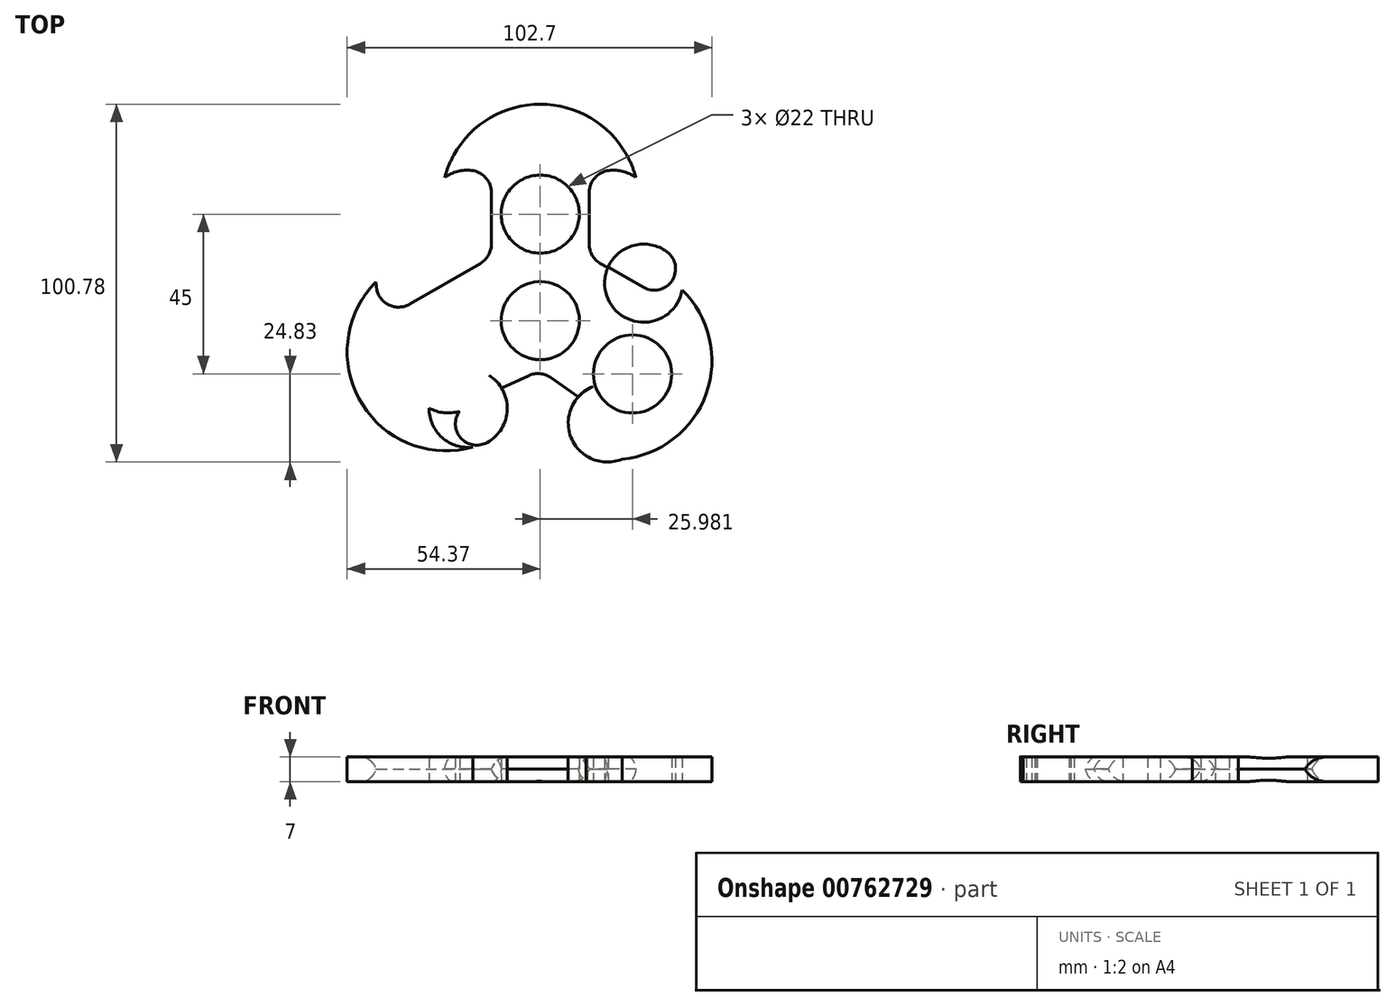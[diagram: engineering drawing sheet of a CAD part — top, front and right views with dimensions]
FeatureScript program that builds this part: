
annotation { "Feature Type Name" : "Feature", "Feature Type Description" : "" }
export const myFeature = defineFeature(function(context is Context, id is Id, definition is map)
    precondition{}
    {
        {
            var Q0;
            Q0=qCreatedBy(makeId("Top.planeOp"),FACE);
            var sketch = newSketch(context, id + "F0", { "sketchPlane" : qUnion([Q0])});
            skCircle(sketch, "E0", {"center": v(0, 0) * mm, "radius": 11 * mm});
            skCircle(sketch, "E1", {"center": v(0, 30) * mm, "radius": 11 * mm});
            skLineSegment(sketch, "E2", {"start": v(0, 30) * mm, "end": v(0, 0) * mm, "construction": true});
            skLineSegment(sketch, "E3", {"start": v(0, 0) * mm, "end": v(25.98, -15) * mm, "construction": true});
            skLineSegment(sketch, "E4", {"start": v(0, 0) * mm, "end": v(-25.98, -15) * mm, "construction": true});
            skCircle(sketch, "E5", {"center": v(-25.98, -15) * mm, "radius": 11 * mm});
            skCircle(sketch, "E6", {"center": v(25.98, -15) * mm, "radius": 11 * mm});
            skLineSegment(sketch, "E7", {"start": v(-36.93, 4.84) * mm, "end": v(-17, 16.35) * mm});
            skLineSegment(sketch, "E8", {"start": v(-20.4, -23.6) * mm, "end": v(-3.15, -15.68) * mm});
            skLineSegment(sketch, "E9", {"start": v(2.83, -16.23) * mm, "end": v(19.2, -27.83) * mm});
            skLineSegment(sketch, "E10", {"start": v(29.1, 9.37) * mm, "end": v(17, 16.35) * mm});
            skLineSegment(sketch, "E11", {"start": v(-14, 36.1) * mm, "end": v(-14, 21.55) * mm});
            skLineSegment(sketch, "E12", {"start": v(14, 36.1) * mm, "end": v(14, 21.55) * mm});
            skPoint(sketch, "E13.visualSharp", {"position": v(-14, 18.08) * mm});
            skArc(sketch, "E13.filletArc", {"start": v(-17, 16.35) * mm, "mid": v(-14.8, 18.55) * mm, "end": v(-14, 21.55) * mm});
            skPoint(sketch, "E14.visualSharp", {"position": v(14, 18.08) * mm});
            skArc(sketch, "E14.filletArc", {"start": v(14, 21.55) * mm, "mid": v(14.8, 18.55) * mm, "end": v(17, 16.35) * mm});
            skPoint(sketch, "E15.visualSharp", {"position": v(0, -14.23) * mm});
            skArc(sketch, "E15.filletArc", {"start": v(2.83, -16.23) * mm, "mid": v(-0.09, -15.15) * mm, "end": v(-3.15, -15.68) * mm});
            skArc(sketch, "E16", {"start": v(-46, 11.15) * mm, "mid": v(-50.64, -22.7) * mm, "end": v(-19, -35.61) * mm});
            skArc(sketch, "E17", {"start": v(12.95, -38.1) * mm, "mid": v(44.6, -25.2) * mm, "end": v(39.95, 8.66) * mm});
            skArc(sketch, "E18", {"start": v(27, 40) * mm, "mid": v(0, 60.95) * mm, "end": v(-27, 40) * mm});
            skArc(sketch, "E19", {"start": v(-46, 11.15) * mm, "mid": v(-45.97, 10.08) * mm, "end": v(-45.84, 9.01) * mm});
            skArc(sketch, "E20", {"start": v(-14.96, -34.3) * mm, "mid": v(-23.72, -14.23) * mm, "end": v(-19, -35.61) * mm});
            skArc(sketch, "E21", {"start": v(12.95, -38.1) * mm, "mid": v(25.3, -19.9) * mm, "end": v(11.97, -37.4) * mm});
            skArc(sketch, "E22", {"start": v(35.66, 19.39) * mm, "mid": v(18.9, 6.46) * mm, "end": v(39.95, 8.66) * mm});
            skArc(sketch, "E23", {"start": v(27, 40) * mm, "mid": v(23.4, 41.74) * mm, "end": v(19.4, 42.07) * mm});
            skArc(sketch, "E24", {"start": v(-19.4, 42.07) * mm, "mid": v(-23.4, 41.74) * mm, "end": v(-27, 40) * mm});
            skPoint(sketch, "E25.visualSharp", {"position": v(-14, 40) * mm});
            skArc(sketch, "E25.filletArc", {"start": v(-14, 36.1) * mm, "mid": v(-15.55, 40.13) * mm, "end": v(-19.4, 42.07) * mm});
            skPoint(sketch, "E26.visualSharp", {"position": v(14, 40) * mm});
            skArc(sketch, "E26.filletArc", {"start": v(19.4, 42.07) * mm, "mid": v(15.55, 40.13) * mm, "end": v(14, 36.1) * mm});
            skPoint(sketch, "E27.visualSharp", {"position": v(38.08, 4.18) * mm});
            skArc(sketch, "E27.filletArc", {"start": v(29.1, 9.37) * mm, "mid": v(37.1, 11.28) * mm, "end": v(35.66, 19.39) * mm});
            skPoint(sketch, "E28.visualSharp", {"position": v(-41.64, 2.12) * mm});
            skArc(sketch, "E28.filletArc", {"start": v(-45.84, 9.01) * mm, "mid": v(-42.47, 4.6) * mm, "end": v(-36.93, 4.84) * mm});
            skPoint(sketch, "E29.visualSharp", {"position": v(-30.7, -28.35) * mm});
            skArc(sketch, "E29.filletArc", {"start": v(-20.4, -23.6) * mm, "mid": v(-23.23, -31.78) * mm, "end": v(-14.96, -34.3) * mm});
            skPoint(sketch, "E30.visualSharp", {"position": v(28.4, -34.34) * mm});
            skArc(sketch, "E30.filletArc", {"start": v(11.97, -37.4) * mm, "mid": v(20.52, -36.34) * mm, "end": v(19.2, -27.83) * mm});
            skSolve(sketch);
        }
        {
            var Q0;
            Q0 = qSketchRegion(id + "F0", true);
            extrude(context, id + "F1", {"entities" : qUnion([Q0]), "depth" : 7 * mm, "offsetDistance" : 25 * mm});
        }
        {
            var Q0;
            Q0=makeQuery(id+"F1.opExtrude","CAP_EDGE",EDGE,{"disambiguationData":[OSD([sQuery(id+"F0.wireOp",EDGE,"E9")])],"isStart":false});
            var Q1;
            Q1=makeQuery(id+"F1.opExtrude","CAP_EDGE",EDGE,{"disambiguationData":[OSD([sQuery(id+"F0.wireOp",EDGE,"E7")])],"isStart":false});
            var Q2;
            Q2=makeQuery(id+"F1.opExtrude","CAP_EDGE",EDGE,{"disambiguationData":[OSD([sQuery(id+"F0.wireOp",EDGE,"E10")])],"isStart":false});
            var Q3;
            Q3=makeQuery(id+"F1.opExtrude","CAP_EDGE",EDGE,{"disambiguationData":[OSD([sQuery(id+"F0.wireOp",EDGE,"E10")])],"isStart":true});
            var Q4;
            Q4=makeQuery(id+"F1.opExtrude","CAP_EDGE",EDGE,{"disambiguationData":[OSD([sQuery(id+"F0.wireOp",EDGE,"E7")])],"isStart":true});
            var Q5;
            Q5=makeQuery(id+"F1.opExtrude","CAP_EDGE",EDGE,{"disambiguationData":[OSD([sQuery(id+"F0.wireOp",EDGE,"E8")])],"isStart":true});
            fillet(context, id + "F2", {"entities" : qUnion([Q0, Q1, Q2, Q3, Q4, Q5]), "radius" : 5 * mm, "tangentPropagation" : true, "allowEdgeOverflow" : false});
        }
    });
